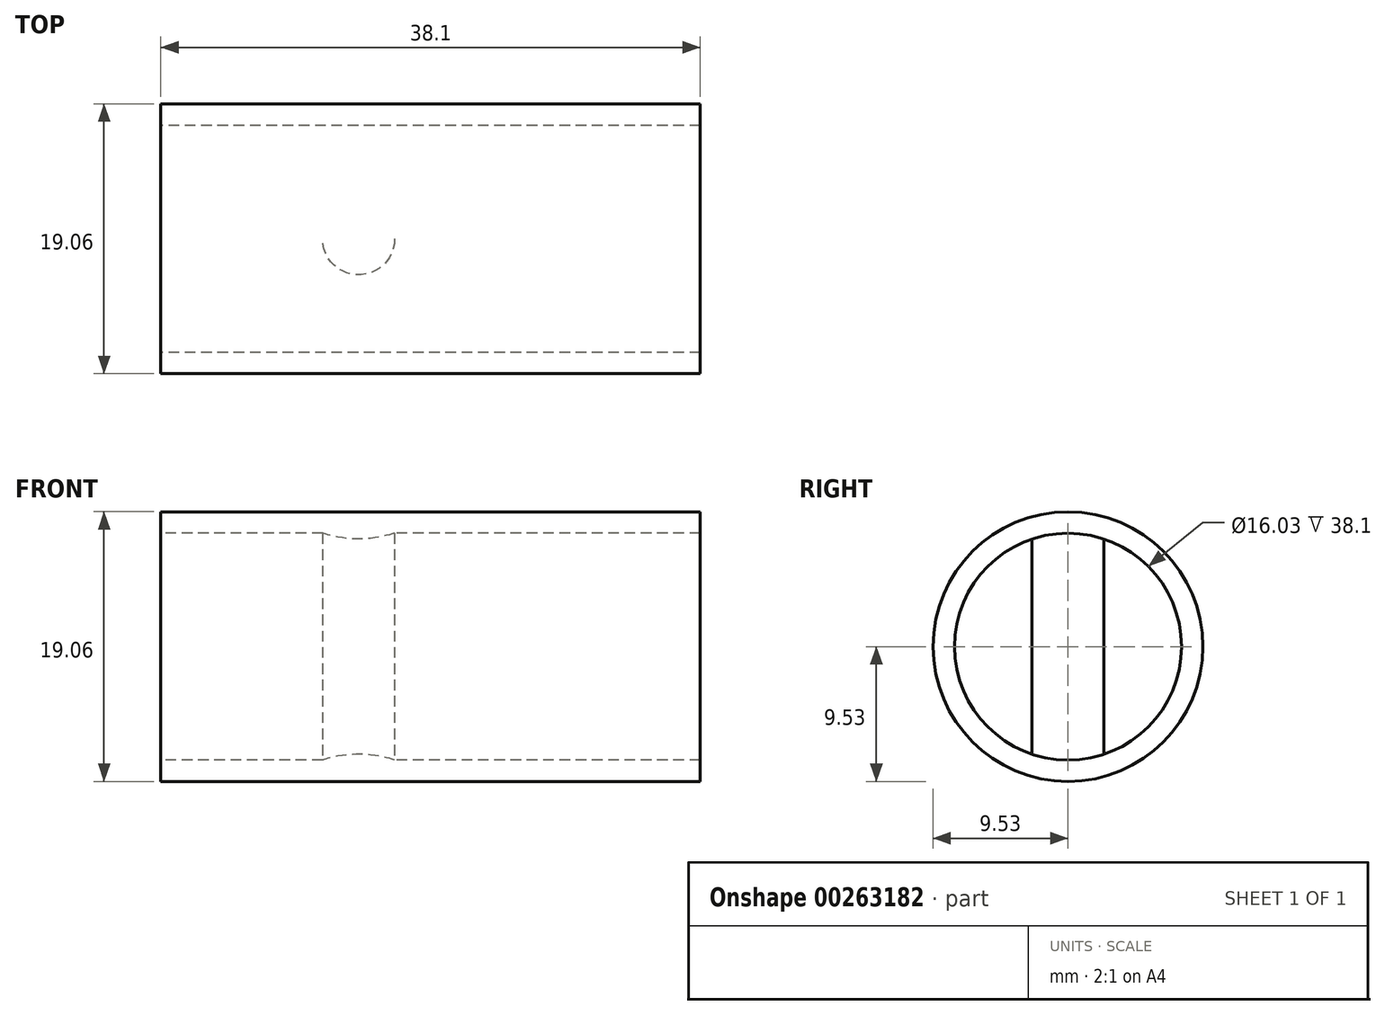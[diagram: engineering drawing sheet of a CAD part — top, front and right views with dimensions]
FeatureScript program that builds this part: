
annotation { "Feature Type Name" : "Feature", "Feature Type Description" : "" }
export const myFeature = defineFeature(function(context is Context, id is Id, definition is map)
    precondition{}
    {
        {
            var Q0;
            Q0=qCreatedBy(makeId("Right.planeOp"),FACE);
            var sketch = newSketch(context, id + "F0", { "sketchPlane" : qUnion([Q0])});
            skCircle(sketch, "E0", {"center": v(0, 0) * mm, "radius": 9.53 * mm});
            skCircle(sketch, "E1", {"center": v(0, 0) * mm, "radius": 8.01 * mm});
            skSolve(sketch);
        }
        {
            var Q0;
            Q0 = qSketchRegion(id + "F0", true);
            extrude(context, id + "F1", {"entities" : qUnion([Q0]), "endBound" : BoundingType.SYMMETRIC, "depth" : 38.1 * mm});
        }
        {
            var Q0;
            Q0=qCreatedBy(makeId("Top.planeOp"),FACE);
            var sketch = newSketch(context, id + "F2", { "sketchPlane" : qUnion([Q0])});
            skCircle(sketch, "E2", {"center": v(-5.08, 0) * mm, "radius": 2.54 * mm});
            skSolve(sketch);
        }
        {
            var Q0;
            Q0 = qSketchRegion(id + "F2", true);
            extrude(context, id + "F3", {"entities" : qUnion([Q0]), "operationType" : NewBodyOperationType.ADD, "endBound" : BoundingType.SYMMETRIC, "depth" : 17.6 * mm});
        }
    });
